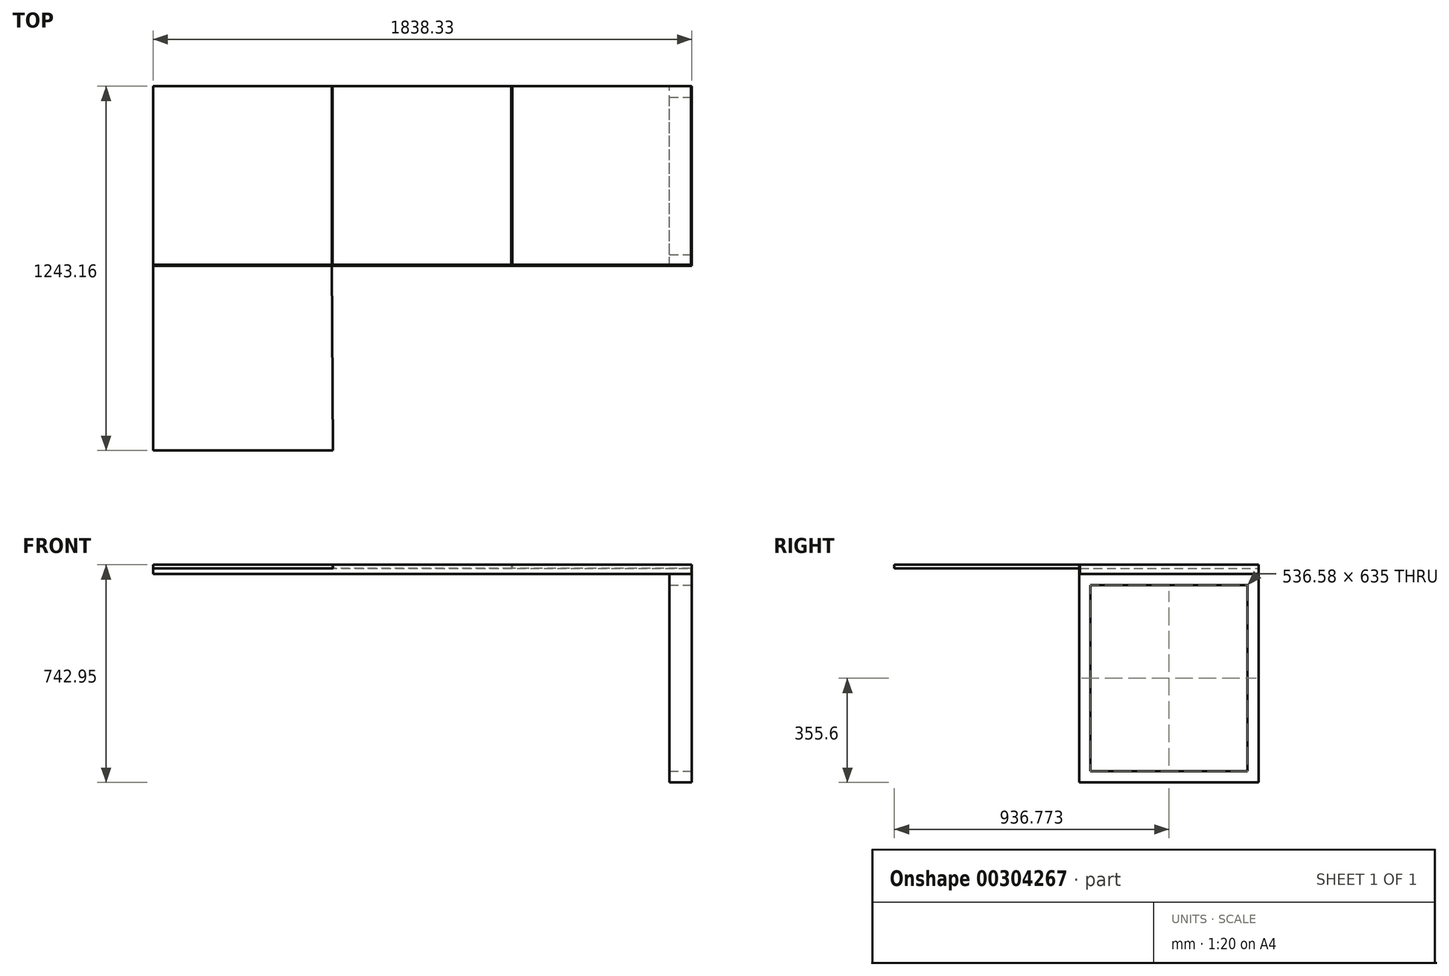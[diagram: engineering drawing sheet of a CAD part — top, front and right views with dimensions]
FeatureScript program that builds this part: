
annotation { "Feature Type Name" : "Feature", "Feature Type Description" : "" }
export const myFeature = defineFeature(function(context is Context, id is Id, definition is map)
    precondition{}
    {
        {
            var Q0;
            Q0=qCreatedBy(makeId("Top.planeOp"),FACE);
            var sketch = newSketch(context, id + "F0", { "sketchPlane" : qUnion([Q0])});
            skLineSegment(sketch, "E0.bottom", {"start": v(609.6, -304.8) * mm, "end": v(0, -304.8) * mm, "construction": true});
            skLineSegment(sketch, "E0.top", {"start": v(609.6, 304.8) * mm, "end": v(0, 304.8) * mm});
            skLineSegment(sketch, "E0.left", {"start": v(609.6, -304.8) * mm, "end": v(609.6, 304.8) * mm});
            skLineSegment(sketch, "E0.right", {"start": v(0, -304.8) * mm, "end": v(0, 304.8) * mm});
            skPoint(sketch, "E0.middle", {"position": v(304.8, 0) * mm});
            skLineSegment(sketch, "E1.bottom", {"start": v(1222.37, -304.8) * mm, "end": v(612.77, -304.8) * mm});
            skLineSegment(sketch, "E1.top", {"start": v(1222.38, 304.8) * mm, "end": v(612.77, 304.8) * mm});
            skLineSegment(sketch, "E1.left", {"start": v(1222.37, -304.8) * mm, "end": v(1222.38, 304.8) * mm});
            skLineSegment(sketch, "E1.right", {"start": v(612.77, -304.8) * mm, "end": v(612.78, 304.8) * mm});
            skPoint(sketch, "E1.middle", {"position": v(917.57, 0) * mm});
            skLineSegment(sketch, "E2.bottom", {"start": v(1835.15, -304.8) * mm, "end": v(1225.55, -304.8) * mm});
            skLineSegment(sketch, "E2.top", {"start": v(1835.15, 304.8) * mm, "end": v(1225.55, 304.8) * mm});
            skLineSegment(sketch, "E2.left", {"start": v(1835.15, -304.8) * mm, "end": v(1835.15, 304.8) * mm});
            skLineSegment(sketch, "E2.right", {"start": v(1225.55, -304.8) * mm, "end": v(1225.55, 304.8) * mm});
            skPoint(sketch, "E2.middle", {"position": v(1530.35, 0) * mm});
            skLineSegment(sketch, "E3", {"start": v(609.6, 304.8) * mm, "end": v(612.77, 304.8) * mm, "construction": true});
            skLineSegment(sketch, "E4", {"start": v(1225.55, 304.8) * mm, "end": v(1222.38, 304.8) * mm, "construction": true});
            skLineSegment(sketch, "E5", {"start": v(0, -304.8) * mm, "end": v(0, -938.36) * mm});
            skLineSegment(sketch, "E6", {"start": v(0, -938.36) * mm, "end": v(613.72, -938.36) * mm});
            skLineSegment(sketch, "E7", {"start": v(613.72, -938.36) * mm, "end": v(609.6, -304.8) * mm});
            skSolve(sketch);
        }
        {
            var Q0;
            Q0 = qSketchRegion(id + "F0", true);
            extrude(context, id + "F1", {"entities" : qUnion([Q0]), "depth" : 12.7 * mm});
        }
        {
            var Q0;
            Q0=qCreatedBy(makeId("Top.planeOp"),FACE);
            var sketch = newSketch(context, id + "F2", { "sketchPlane" : qUnion([Q0])});
            skLineSegment(sketch, "E8.bottom", {"start": v(0, -304.8) * mm, "end": v(1835.15, -304.8) * mm});
            skLineSegment(sketch, "E8.top", {"start": v(0, 304.8) * mm, "end": v(1835.15, 304.8) * mm});
            skLineSegment(sketch, "E8.left", {"start": v(0, -304.8) * mm, "end": v(0, 304.8) * mm});
            skLineSegment(sketch, "E8.right", {"start": v(1835.15, -304.8) * mm, "end": v(1835.15, 304.8) * mm});
            skSolve(sketch);
        }
        {
            var Q0;
            Q0 = qSketchRegion(id + "F2", true);
            extrude(context, id + "F3", {"entities" : qUnion([Q0]), "oppositeDirection" : true, "depth" : 19.05 * mm});
        }
        {
            var Q0;
            Q0=makeQuery(id+"F3.opExtrude","SWEPT_FACE",FACE,{"disambiguationData":[OSD([sQuery(id+"F2.wireOp",EDGE,"E8.right")])]});
            var sketch = newSketch(context, id + "F4", { "sketchPlane" : qUnion([Q0])});
            skLineSegment(sketch, "E9.bottom", {"start": v(-304.8, 12.7) * mm, "end": v(304.8, 12.7) * mm});
            skLineSegment(sketch, "E9.top", {"start": v(-304.8, -19.05) * mm, "end": v(304.8, -19.05) * mm});
            skLineSegment(sketch, "E9.left", {"start": v(-304.8, 12.7) * mm, "end": v(-304.8, -19.05) * mm});
            skLineSegment(sketch, "E9.right", {"start": v(304.8, 12.7) * mm, "end": v(304.8, -19.05) * mm});
            skSolve(sketch);
        }
        {
            var Q0;
            Q0 = qSketchRegion(id + "F4", true);
            extrude(context, id + "F5", {"entities" : qUnion([Q0]), "depth" : 3.17 * mm});
        }
        {
            var Q0;
            Q0=makeQuery(id+"F3.opExtrude","SWEPT_FACE",FACE,{"disambiguationData":[OSD([sQuery(id+"F2.wireOp",EDGE,"E8.bottom")])]});
            var sketch = newSketch(context, id + "F6", { "sketchPlane" : qUnion([Q0])});
            skLineSegment(sketch, "E10.bottom", {"start": v(1838.32, -19.05) * mm, "end": v(0, -19.05) * mm});
            skLineSegment(sketch, "E10.top", {"start": v(1838.32, 12.7) * mm, "end": v(0, 12.7) * mm});
            skLineSegment(sketch, "E10.left", {"start": v(1838.32, -19.05) * mm, "end": v(1838.32, 12.7) * mm});
            skLineSegment(sketch, "E10.right", {"start": v(0, -19.05) * mm, "end": v(0, 12.7) * mm});
            skSolve(sketch);
        }
        {
            var Q0;
            Q0 = qSketchRegion(id + "F6", true);
            extrude(context, id + "F7", {"entities" : qUnion([Q0]), "depth" : 3.17 * mm});
        }
        {
            var Q0;
            Q0=qCreatedBy(makeId("Top.planeOp"),FACE);
            var sketch = newSketch(context, id + "F8", { "sketchPlane" : qUnion([Q0])});
            skLineSegment(sketch, "E11.bottom", {"start": v(609.6, 304.8) * mm, "end": v(612.77, 304.8) * mm});
            skLineSegment(sketch, "E11.top", {"start": v(609.6, -304.8) * mm, "end": v(612.77, -304.8) * mm});
            skLineSegment(sketch, "E11.left", {"start": v(609.6, 304.8) * mm, "end": v(609.6, -304.8) * mm});
            skLineSegment(sketch, "E11.right", {"start": v(612.77, 304.8) * mm, "end": v(612.77, -304.8) * mm});
            skLineSegment(sketch, "E12.bottom", {"start": v(1222.38, -304.8) * mm, "end": v(1225.55, -304.8) * mm});
            skLineSegment(sketch, "E12.top", {"start": v(1222.38, 304.8) * mm, "end": v(1225.55, 304.8) * mm});
            skLineSegment(sketch, "E12.left", {"start": v(1222.38, -304.8) * mm, "end": v(1222.38, 304.8) * mm});
            skLineSegment(sketch, "E12.right", {"start": v(1225.55, -304.8) * mm, "end": v(1225.55, 304.8) * mm});
            skSolve(sketch);
        }
        {
            var Q0;
            Q0 = qSketchRegion(id + "F8", true);
            extrude(context, id + "F9", {"entities" : qUnion([Q0]), "depth" : 12.7 * mm});
        }
        {
            var Q0;
            Q0=makeQuery(id+"F5.opExtrude","CAP_FACE",FACE,{"disambiguationData":[OSD([sQuery(id+"F4.wireOp",EDGE,"E9.bottom"),sQuery(id+"F4.wireOp",EDGE,"E9.top"),sQuery(id+"F4.wireOp",EDGE,"E9.left"),sQuery(id+"F4.wireOp",EDGE,"E9.right")])],"isStart":false});
            var sketch = newSketch(context, id + "F10", { "sketchPlane" : qUnion([Q0])});
            skLineSegment(sketch, "E13.bottom", {"start": v(-307.98, -730.25) * mm, "end": v(304.8, -730.25) * mm});
            skLineSegment(sketch, "E13.top", {"start": v(-307.98, -19.05) * mm, "end": v(304.8, -19.05) * mm});
            skLineSegment(sketch, "E13.left", {"start": v(-307.98, -730.25) * mm, "end": v(-307.98, -19.05) * mm});
            skLineSegment(sketch, "E13.right", {"start": v(304.8, -730.25) * mm, "end": v(304.8, -19.05) * mm});
            skLineSegment(sketch, "E14.0", {"start": v(-269.88, -57.15) * mm, "end": v(266.7, -57.15) * mm});
            skLineSegment(sketch, "E14.1", {"start": v(-269.88, -692.15) * mm, "end": v(-269.88, -57.15) * mm});
            skLineSegment(sketch, "E14.2", {"start": v(-269.88, -692.15) * mm, "end": v(266.7, -692.15) * mm});
            skLineSegment(sketch, "E14.3", {"start": v(266.7, -692.15) * mm, "end": v(266.7, -57.15) * mm});
            skSolve(sketch);
        }
        {
            var Q0;
            Q0 = qSketchRegion(id + "F10", true);
            extrude(context, id + "F11", {"entities" : qUnion([Q0]), "oppositeDirection" : true, "depth" : 76.2 * mm});
        }
    });
